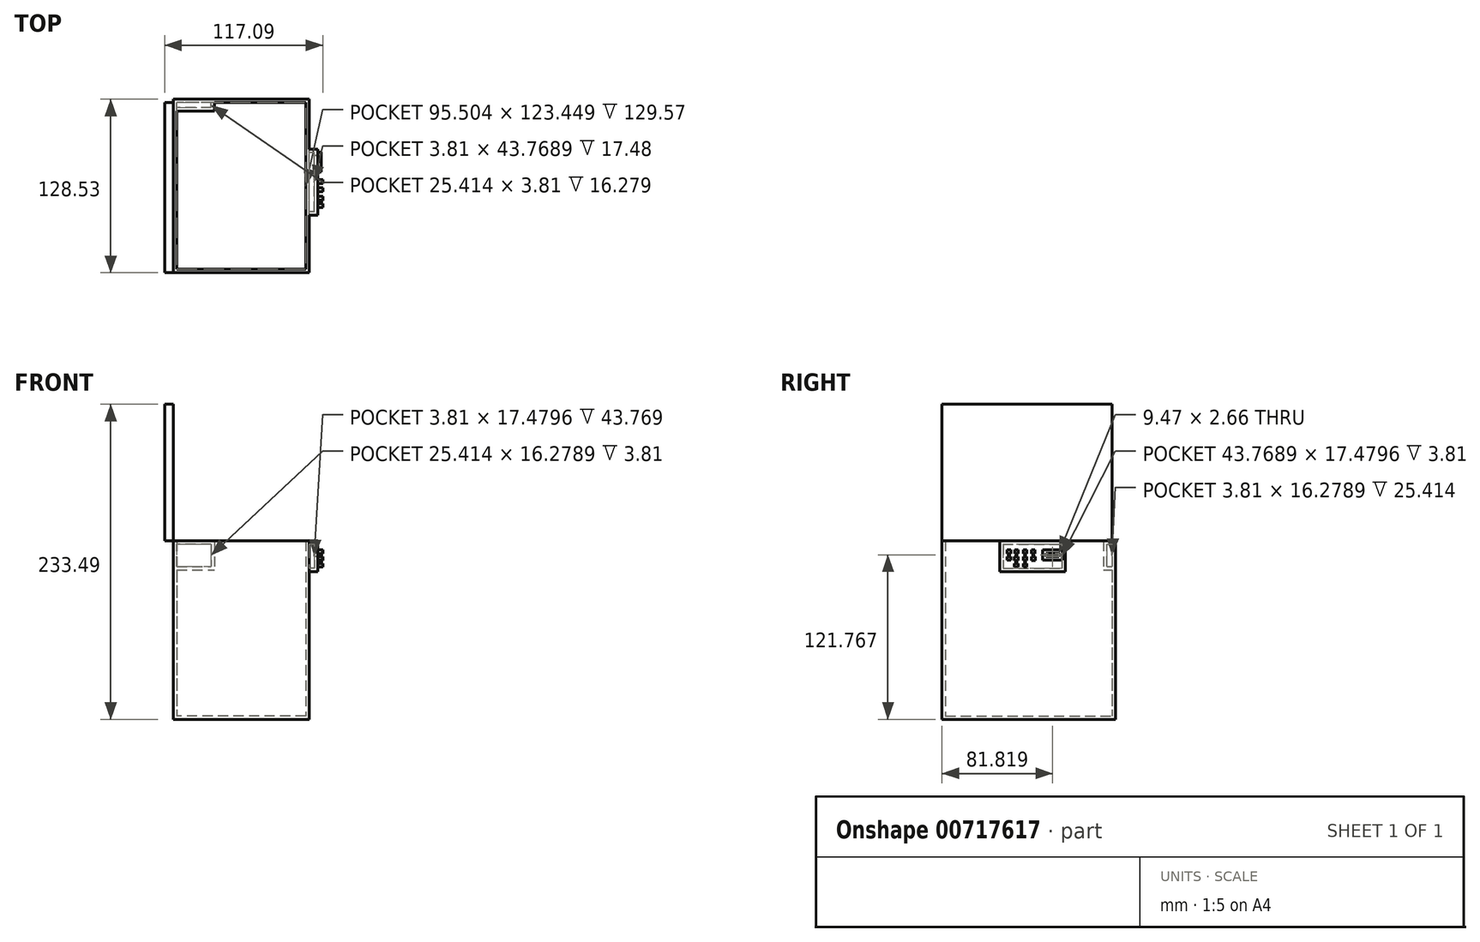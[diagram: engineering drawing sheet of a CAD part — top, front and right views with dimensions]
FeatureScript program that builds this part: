
annotation { "Feature Type Name" : "Feature", "Feature Type Description" : "" }
export const myFeature = defineFeature(function(context is Context, id is Id, definition is map)
    precondition{}
    {
        {
            var Q0;
            Q0=qCreatedBy(makeId("Right.planeOp"),FACE);
            var sketch = newSketch(context, id + "F0", { "sketchPlane" : qUnion([Q0])});
            skLineSegment(sketch, "E0.bottom", {"start": v(-110.63, 125.54) * mm, "end": v(17.9, 125.54) * mm});
            skLineSegment(sketch, "E0.top", {"start": v(-110.63, -6.57) * mm, "end": v(17.9, -6.57) * mm});
            skLineSegment(sketch, "E0.left", {"start": v(-110.63, 125.54) * mm, "end": v(-110.63, -6.57) * mm});
            skLineSegment(sketch, "E0.right", {"start": v(17.9, 125.54) * mm, "end": v(17.9, -6.57) * mm});
            skSolve(sketch);
        }
        {
            var Q0;
            Q0=makeQuery(id+"F0.imprint","IMPRINT",FACE,{"disambiguationData":[TD([[makeQuery(id+"F0.imprint","IMPRINT",EDGE,{"derivedFrom":sQuery(id+"F0.wireOp",EDGE,"E0.bottom")}),-1.0]])]});
            extrude(context, id + "F1", {"entities" : qUnion([Q0]), "depth" : 100.58 * mm, "offsetDistance" : 25.4 * mm});
        }
        {
            var Q0;
            Q0=makeQuery(id+"F1.opExtrude","SWEPT_FACE",FACE,{"disambiguationData":[OSD([sQuery(id+"F0.wireOp",EDGE,"E0.bottom")])]});
            shell(context, id + "F2", {"entities" : qUnion([Q0]), "thickness" : 2.54 * mm});
        }
        {
            var Q0;
            Q0=makeQuery(id+"F1.opExtrude","CAP_FACE",FACE,{"disambiguationData":[OSD([sQuery(id+"F0.wireOp",EDGE,"E0.bottom"),sQuery(id+"F0.wireOp",EDGE,"E0.top"),sQuery(id+"F0.wireOp",EDGE,"E0.left"),sQuery(id+"F0.wireOp",EDGE,"E0.right")])],"isStart":true});
            var sketch = newSketch(context, id + "F3", { "sketchPlane" : qUnion([Q0])});
            skLineSegment(sketch, "E1.bottom", {"start": v(110.63, 125.54) * mm, "end": v(-15.33, 125.54) * mm});
            skLineSegment(sketch, "E1.top", {"start": v(110.63, 226.92) * mm, "end": v(-15.33, 226.92) * mm});
            skLineSegment(sketch, "E1.left", {"start": v(110.63, 125.54) * mm, "end": v(110.63, 226.92) * mm});
            skLineSegment(sketch, "E1.right", {"start": v(-15.33, 125.54) * mm, "end": v(-15.33, 226.92) * mm});
            skSolve(sketch);
        }
        {
            var Q0;
            Q0=makeQuery(id+"F3.imprint","IMPRINT",FACE,{"disambiguationData":[TD([[makeQuery(id+"F3.imprint","IMPRINT",EDGE,{"derivedFrom":sQuery(id+"F3.wireOp",EDGE,"E1.bottom")}),-1.0]])]});
            extrude(context, id + "F4", {"entities" : qUnion([Q0]), "depth" : 6.35 * mm, "offsetDistance" : 25.4 * mm});
        }
        {
            var Q0;
            Q0=makeQuery(id+"F2.opShell","OFFSET_FACE",FACE,{"disambiguationData":[OSD([sQuery(id+"F0.wireOp",EDGE,"E0.right")])]});
            var sketch = newSketch(context, id + "F5", { "sketchPlane" : qUnion([Q0])});
            skLineSegment(sketch, "E2.bottom", {"start": v(2.54, 125.54) * mm, "end": v(30.5, 125.54) * mm});
            skLineSegment(sketch, "E2.top", {"start": v(2.54, 104.19) * mm, "end": v(30.5, 104.19) * mm});
            skLineSegment(sketch, "E2.left", {"start": v(2.54, 125.54) * mm, "end": v(2.54, 104.19) * mm});
            skLineSegment(sketch, "E2.right", {"start": v(30.5, 125.54) * mm, "end": v(30.5, 104.19) * mm});
            skSolve(sketch);
        }
        {
            var Q0;
            Q0=makeQuery(id+"F5.imprint","IMPRINT",FACE,{"disambiguationData":[TD([[makeQuery(id+"F5.imprint","IMPRINT",EDGE,{"derivedFrom":sQuery(id+"F5.wireOp",EDGE,"E2.bottom")}),1.0]])]});
            extrude(context, id + "F6", {"entities" : qUnion([Q0]), "operationType" : NewBodyOperationType.ADD, "depth" : 6.35 * mm, "offsetDistance" : 25.4 * mm});
        }
        {
            var Q0;
            Q0=makeQuery(id+"F1.opExtrude","CAP_FACE",FACE,{"disambiguationData":[OSD([sQuery(id+"F0.wireOp",EDGE,"E0.bottom"),sQuery(id+"F0.wireOp",EDGE,"E0.top"),sQuery(id+"F0.wireOp",EDGE,"E0.left"),sQuery(id+"F0.wireOp",EDGE,"E0.right")])],"isStart":false});
            var sketch = newSketch(context, id + "F7", { "sketchPlane" : qUnion([Q0])});
            skLineSegment(sketch, "E3.bottom", {"start": v(-68, 125.54) * mm, "end": v(-19.15, 125.54) * mm});
            skLineSegment(sketch, "E3.top", {"start": v(-68, 102.98) * mm, "end": v(-19.15, 102.98) * mm});
            skLineSegment(sketch, "E3.left", {"start": v(-68, 125.54) * mm, "end": v(-68, 102.98) * mm});
            skLineSegment(sketch, "E3.right", {"start": v(-19.15, 125.54) * mm, "end": v(-19.15, 102.98) * mm});
            skSolve(sketch);
        }
        {
            var Q0;
            Q0=makeQuery(id+"F7.imprint","IMPRINT",FACE,{"disambiguationData":[TD([[makeQuery(id+"F7.imprint","IMPRINT",EDGE,{"derivedFrom":sQuery(id+"F7.wireOp",EDGE,"E3.bottom")}),-1.0]])]});
            extrude(context, id + "F8", {"entities" : qUnion([Q0]), "operationType" : NewBodyOperationType.ADD, "depth" : 6.35 * mm, "offsetDistance" : 25.4 * mm});
        }
        {
            var Q0;
            Q0=makeQuery(id+"F8.opExtrude","CAP_FACE",FACE,{"disambiguationData":[OSD([sQuery(id+"F7.wireOp",EDGE,"E3.bottom"),sQuery(id+"F7.wireOp",EDGE,"E3.top"),sQuery(id+"F7.wireOp",EDGE,"E3.left"),sQuery(id+"F7.wireOp",EDGE,"E3.right")])],"isStart":false});
            var sketch = newSketch(context, id + "F9", { "sketchPlane" : qUnion([Q0])});
            skLineSegment(sketch, "E4.bottom", {"start": v(-62.32, 119.07) * mm, "end": v(-59.56, 119.07) * mm});
            skLineSegment(sketch, "E4.top", {"start": v(-62.32, 116.3) * mm, "end": v(-59.56, 116.3) * mm});
            skLineSegment(sketch, "E4.left", {"start": v(-62.32, 119.07) * mm, "end": v(-62.32, 116.3) * mm});
            skLineSegment(sketch, "E4.right", {"start": v(-59.56, 119.07) * mm, "end": v(-59.56, 116.3) * mm});
            skLineSegment(sketch, "E5.bottom", {"start": v(-56.8, 119.07) * mm, "end": v(-54.17, 119.07) * mm});
            skLineSegment(sketch, "E5.top", {"start": v(-56.8, 116.3) * mm, "end": v(-54.17, 116.3) * mm});
            skLineSegment(sketch, "E5.left", {"start": v(-56.8, 119.07) * mm, "end": v(-56.8, 116.3) * mm});
            skLineSegment(sketch, "E5.right", {"start": v(-54.17, 119.07) * mm, "end": v(-54.17, 116.3) * mm});
            skLineSegment(sketch, "E6.bottom", {"start": v(-50.49, 119.07) * mm, "end": v(-47.73, 119.07) * mm});
            skLineSegment(sketch, "E6.top", {"start": v(-50.49, 116.3) * mm, "end": v(-47.73, 116.3) * mm});
            skLineSegment(sketch, "E6.left", {"start": v(-50.49, 119.07) * mm, "end": v(-50.49, 116.3) * mm});
            skLineSegment(sketch, "E6.right", {"start": v(-47.73, 119.07) * mm, "end": v(-47.73, 116.3) * mm});
            skLineSegment(sketch, "E7.bottom", {"start": v(-44.44, 119.07) * mm, "end": v(-41.67, 119.07) * mm});
            skLineSegment(sketch, "E7.top", {"start": v(-44.44, 116.3) * mm, "end": v(-41.67, 116.3) * mm});
            skLineSegment(sketch, "E7.left", {"start": v(-44.44, 119.07) * mm, "end": v(-44.44, 116.3) * mm});
            skLineSegment(sketch, "E7.right", {"start": v(-41.67, 119.07) * mm, "end": v(-41.67, 116.3) * mm});
            skLineSegment(sketch, "E8.bottom", {"start": v(-62.44, 113.99) * mm, "end": v(-59.68, 113.99) * mm});
            skLineSegment(sketch, "E8.top", {"start": v(-62.44, 111.36) * mm, "end": v(-59.68, 111.36) * mm});
            skLineSegment(sketch, "E8.left", {"start": v(-62.44, 113.99) * mm, "end": v(-62.44, 111.36) * mm});
            skLineSegment(sketch, "E8.right", {"start": v(-59.68, 113.99) * mm, "end": v(-59.68, 111.36) * mm});
            skLineSegment(sketch, "E9.bottom", {"start": v(-56.92, 113.99) * mm, "end": v(-54.29, 113.99) * mm});
            skLineSegment(sketch, "E9.top", {"start": v(-56.92, 111.22) * mm, "end": v(-54.29, 111.22) * mm});
            skLineSegment(sketch, "E9.left", {"start": v(-56.92, 113.99) * mm, "end": v(-56.92, 111.22) * mm});
            skLineSegment(sketch, "E9.right", {"start": v(-54.29, 113.99) * mm, "end": v(-54.29, 111.22) * mm});
            skLineSegment(sketch, "E10.bottom", {"start": v(-50.47, 113.99) * mm, "end": v(-47.7, 113.99) * mm});
            skLineSegment(sketch, "E10.top", {"start": v(-50.47, 111.22) * mm, "end": v(-47.7, 111.22) * mm});
            skLineSegment(sketch, "E10.left", {"start": v(-50.47, 113.99) * mm, "end": v(-50.47, 111.22) * mm});
            skLineSegment(sketch, "E10.right", {"start": v(-47.7, 113.99) * mm, "end": v(-47.7, 111.22) * mm});
            skLineSegment(sketch, "E11.bottom", {"start": v(-44.42, 113.99) * mm, "end": v(-41.66, 113.99) * mm});
            skLineSegment(sketch, "E11.top", {"start": v(-44.42, 111.22) * mm, "end": v(-41.66, 111.22) * mm});
            skLineSegment(sketch, "E11.left", {"start": v(-44.42, 113.99) * mm, "end": v(-44.42, 111.22) * mm});
            skLineSegment(sketch, "E11.right", {"start": v(-41.66, 113.99) * mm, "end": v(-41.66, 111.22) * mm});
            skLineSegment(sketch, "E12.bottom", {"start": v(-57.2, 108.8) * mm, "end": v(-54.3, 108.8) * mm});
            skLineSegment(sketch, "E12.top", {"start": v(-57.2, 106.18) * mm, "end": v(-54.3, 106.18) * mm});
            skLineSegment(sketch, "E12.left", {"start": v(-57.2, 108.8) * mm, "end": v(-57.2, 106.18) * mm});
            skLineSegment(sketch, "E12.right", {"start": v(-54.3, 108.8) * mm, "end": v(-54.3, 106.18) * mm});
            skLineSegment(sketch, "E13.bottom", {"start": v(-50.49, 108.94) * mm, "end": v(-47.86, 108.94) * mm});
            skLineSegment(sketch, "E13.top", {"start": v(-50.49, 106.18) * mm, "end": v(-47.86, 106.18) * mm});
            skLineSegment(sketch, "E13.left", {"start": v(-50.49, 108.94) * mm, "end": v(-50.49, 106.18) * mm});
            skLineSegment(sketch, "E13.right", {"start": v(-47.86, 108.94) * mm, "end": v(-47.86, 106.18) * mm});
            skPoint(sketch, "E14.oppositeSnap0", {"position": v(-19.15, 114.26) * mm});
            skLineSegment(sketch, "E14.bottom", {"start": v(-36.28, 120.12) * mm, "end": v(-22.47, 120.12) * mm});
            skLineSegment(sketch, "E14.top", {"start": v(-36.28, 114.26) * mm, "end": v(-22.47, 114.26) * mm});
            skLineSegment(sketch, "E14.left", {"start": v(-36.28, 120.12) * mm, "end": v(-36.28, 114.26) * mm});
            skLineSegment(sketch, "E14.right", {"start": v(-22.47, 120.12) * mm, "end": v(-22.47, 114.26) * mm});
            skSolve(sketch);
        }
        {
            var Q0;
            Q0=makeQuery(id+"F9.imprint","IMPRINT",FACE,{"disambiguationData":[TD([[makeQuery(id+"F9.imprint","IMPRINT",EDGE,{"derivedFrom":sQuery(id+"F9.wireOp",EDGE,"E4.bottom")}),-1.0]])]});
            var Q1;
            Q1=makeQuery(id+"F9.imprint","IMPRINT",FACE,{"disambiguationData":[TD([[makeQuery(id+"F9.imprint","IMPRINT",EDGE,{"derivedFrom":sQuery(id+"F9.wireOp",EDGE,"E5.bottom")}),-1.0]])]});
            var Q2;
            Q2=makeQuery(id+"F9.imprint","IMPRINT",FACE,{"disambiguationData":[TD([[makeQuery(id+"F9.imprint","IMPRINT",EDGE,{"derivedFrom":sQuery(id+"F9.wireOp",EDGE,"E6.bottom")}),-1.0]])]});
            var Q3;
            Q3=makeQuery(id+"F9.imprint","IMPRINT",FACE,{"disambiguationData":[TD([[makeQuery(id+"F9.imprint","IMPRINT",EDGE,{"derivedFrom":sQuery(id+"F9.wireOp",EDGE,"E7.bottom")}),-1.0]])]});
            var Q4;
            Q4=makeQuery(id+"F9.imprint","IMPRINT",FACE,{"disambiguationData":[TD([[makeQuery(id+"F9.imprint","IMPRINT",EDGE,{"derivedFrom":sQuery(id+"F9.wireOp",EDGE,"E11.bottom")}),-1.0]])]});
            var Q5;
            Q5=makeQuery(id+"F9.imprint","IMPRINT",FACE,{"disambiguationData":[TD([[makeQuery(id+"F9.imprint","IMPRINT",EDGE,{"derivedFrom":sQuery(id+"F9.wireOp",EDGE,"E10.bottom")}),-1.0]])]});
            var Q6;
            Q6=makeQuery(id+"F9.imprint","IMPRINT",FACE,{"disambiguationData":[TD([[makeQuery(id+"F9.imprint","IMPRINT",EDGE,{"derivedFrom":sQuery(id+"F9.wireOp",EDGE,"E13.bottom")}),-1.0]])]});
            var Q7;
            Q7=makeQuery(id+"F9.imprint","IMPRINT",FACE,{"disambiguationData":[TD([[makeQuery(id+"F9.imprint","IMPRINT",EDGE,{"derivedFrom":sQuery(id+"F9.wireOp",EDGE,"E12.bottom")}),-1.0]])]});
            var Q8;
            Q8=makeQuery(id+"F9.imprint","IMPRINT",FACE,{"disambiguationData":[TD([[makeQuery(id+"F9.imprint","IMPRINT",EDGE,{"derivedFrom":sQuery(id+"F9.wireOp",EDGE,"E9.bottom")}),-1.0]])]});
            var Q9;
            Q9=makeQuery(id+"F9.imprint","IMPRINT",FACE,{"disambiguationData":[TD([[makeQuery(id+"F9.imprint","IMPRINT",EDGE,{"derivedFrom":sQuery(id+"F9.wireOp",EDGE,"E8.bottom")}),-1.0]])]});
            extrude(context, id + "F10", {"entities" : qUnion([Q0, Q1, Q2, Q3, Q4, Q5, Q6, Q7, Q8, Q9]), "operationType" : NewBodyOperationType.ADD, "depth" : 3.8 * mm, "offsetDistance" : 25.4 * mm});
        }
        {
            var Q0;
            Q0=makeQuery(id+"F8.opExtrude","CAP_FACE",FACE,{"disambiguationData":[OSD([sQuery(id+"F7.wireOp",EDGE,"E3.bottom"),sQuery(id+"F7.wireOp",EDGE,"E3.top"),sQuery(id+"F7.wireOp",EDGE,"E3.left"),sQuery(id+"F7.wireOp",EDGE,"E3.right")])],"isStart":false});
            var sketch = newSketch(context, id + "F11", { "sketchPlane" : qUnion([Q0])});
            skLineSegment(sketch, "E15.bottom", {"start": v(-36.55, 119.2) * mm, "end": v(-20.9, 119.2) * mm});
            skLineSegment(sketch, "E15.top", {"start": v(-36.55, 114.46) * mm, "end": v(-20.9, 114.46) * mm});
            skLineSegment(sketch, "E15.left", {"start": v(-36.55, 119.2) * mm, "end": v(-36.55, 114.46) * mm});
            skLineSegment(sketch, "E15.right", {"start": v(-20.9, 119.2) * mm, "end": v(-20.9, 114.46) * mm});
            skSolve(sketch);
        }
        {
            var Q0;
            Q0=makeQuery(id+"F11.imprint","IMPRINT",FACE,{"disambiguationData":[TD([[makeQuery(id+"F11.imprint","IMPRINT",EDGE,{"derivedFrom":sQuery(id+"F11.wireOp",EDGE,"E15.bottom")}),-1.0]])]});
            extrude(context, id + "F12", {"entities" : qUnion([Q0]), "operationType" : NewBodyOperationType.ADD, "depth" : -5.08 * mm, "offsetDistance" : 25.4 * mm});
        }
        {
            var Q0;
            Q0=makeQuery(id+"F8.opExtrude","CAP_FACE",FACE,{"disambiguationData":[OSD([sQuery(id+"F7.wireOp",EDGE,"E3.bottom"),sQuery(id+"F7.wireOp",EDGE,"E3.top"),sQuery(id+"F7.wireOp",EDGE,"E3.left"),sQuery(id+"F7.wireOp",EDGE,"E3.right")])],"isStart":false});
            var sketch = newSketch(context, id + "F13", { "sketchPlane" : qUnion([Q0])});
            skPoint(sketch, "E16.firstSnap0", {"position": v(-43.06, 119.07) * mm});
            skLineSegment(sketch, "E16.bottom", {"start": v(-36.08, 119.07) * mm, "end": v(-21.54, 119.07) * mm});
            skLineSegment(sketch, "E16.top", {"start": v(-36.08, 111.33) * mm, "end": v(-21.54, 111.33) * mm});
            skLineSegment(sketch, "E16.left", {"start": v(-36.08, 119.07) * mm, "end": v(-36.08, 111.33) * mm});
            skLineSegment(sketch, "E16.right", {"start": v(-21.54, 119.07) * mm, "end": v(-21.54, 111.33) * mm});
            skSolve(sketch);
        }
        {
            var Q0;
            Q0=makeQuery(id+"F13.imprint","IMPRINT",FACE,{"disambiguationData":[TD([[makeQuery(id+"F13.imprint","IMPRINT",EDGE,{"derivedFrom":sQuery(id+"F13.wireOp",EDGE,"E16.bottom")}),-1.0]])]});
            extrude(context, id + "F14", {"entities" : qUnion([Q0]), "operationType" : NewBodyOperationType.ADD, "depth" : 2.54 * mm, "offsetDistance" : 25.4 * mm});
        }
        {
            var Q0;
            Q0=makeQuery(id+"F14.opExtrude","CAP_FACE",FACE,{"disambiguationData":[OSD([sQuery(id+"F13.wireOp",EDGE,"E16.bottom"),sQuery(id+"F13.wireOp",EDGE,"E16.top"),sQuery(id+"F13.wireOp",EDGE,"E16.left"),sQuery(id+"F13.wireOp",EDGE,"E16.right")])],"isStart":false});
            shell(context, id + "F15", {"entities" : qUnion([Q0]), "thickness" : 2.54 * mm});
        }
    });
